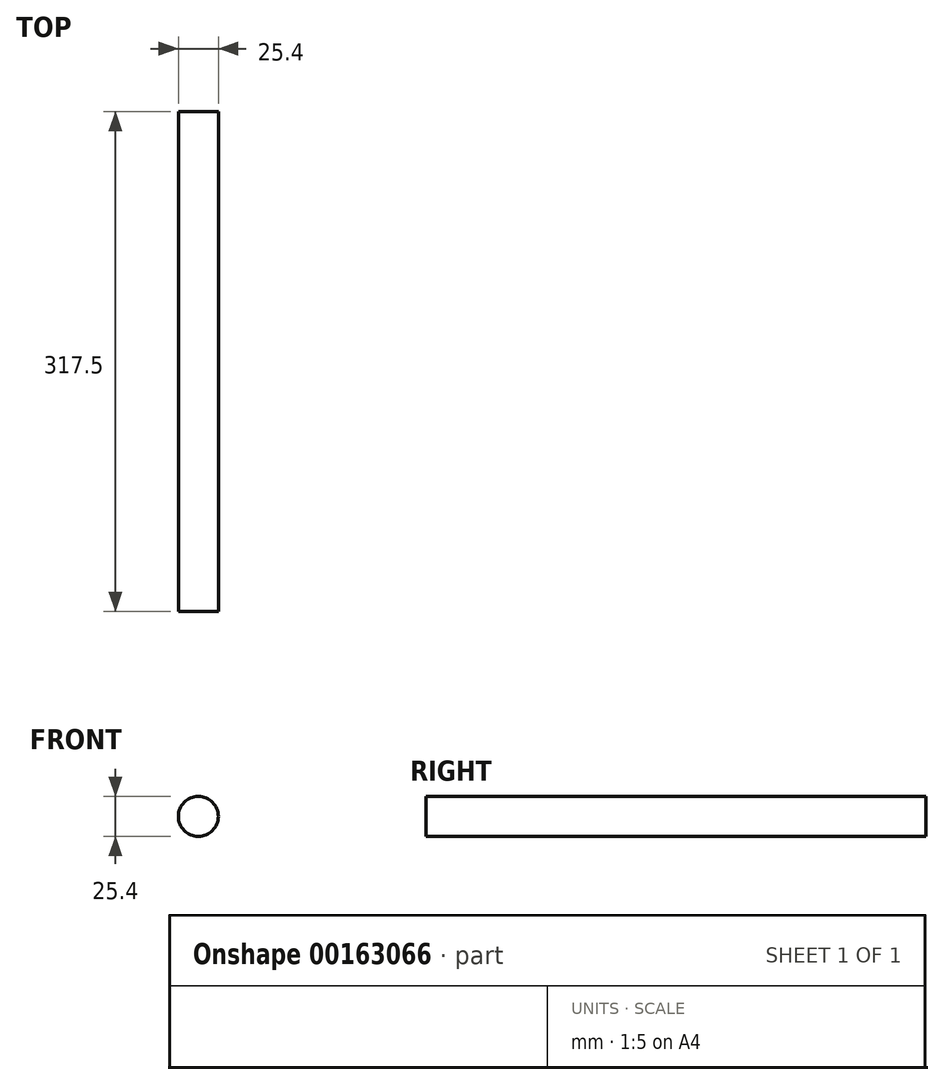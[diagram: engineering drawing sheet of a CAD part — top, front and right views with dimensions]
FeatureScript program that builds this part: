
annotation { "Feature Type Name" : "Feature", "Feature Type Description" : "" }
export const myFeature = defineFeature(function(context is Context, id is Id, definition is map)
    precondition{}
    {
        {
            var Q0;
            Q0=qCreatedBy(makeId("Front.planeOp"),FACE);
            var sketch = newSketch(context, id + "F0", { "sketchPlane" : qUnion([Q0])});
            skCircle(sketch, "E0", {"center": v(0, 0) * mm, "radius": 12.7 * mm});
            skSolve(sketch);
        }
        {
            var Q0;
            Q0=makeQuery(id+"F0.imprint","IMPRINT",FACE,{"disambiguationData":[TD([[makeQuery(id+"F0.imprint","IMPRINT",EDGE,{"derivedFrom":sQuery(id+"F0.wireOp",EDGE,"E0")}),1.0]])]});
            extrude(context, id + "F1", {"entities" : qUnion([Q0]), "depth" : 317.5 * mm});
        }
    });
